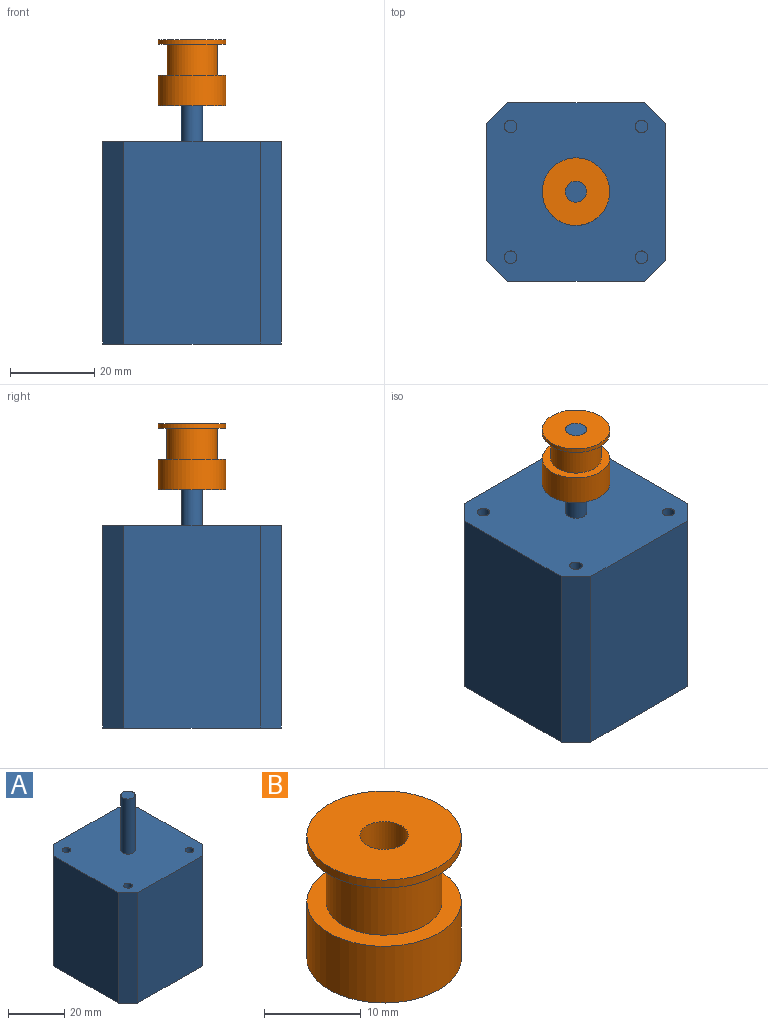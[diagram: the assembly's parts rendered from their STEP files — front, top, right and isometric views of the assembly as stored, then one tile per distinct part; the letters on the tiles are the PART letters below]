
ASSEMBLY  parts=2 mates=1
PART A: 20 faces, bbox 42.3x42.3x72 mm
  f0: plane 48x32.3mm, normal (0,-1,0), area 1550.4mm2, adj f4,f5,f7,f8
  f1: plane 48x32.3mm, normal (1,0,0), area 1550.4mm2, adj f4,f5,f8,f9
  f2: plane 48x32.3mm, normal (0,1,0), area 1550.4mm2, adj f4,f5,f6,f9
  f3: plane 48x32.3mm, normal (-1,0,0), area 1550.4mm2, adj f4,f5,f6,f7
  f4: plane 42.3x42.3mm, normal (0,0,1), area 1691.4mm2, adj f0,f1,f2,f3,f6,f7,f8,f9
  f5: plane 42.3x42.3mm, normal (0,0,-1), area 1739.3mm2, adj f0,f1,f2,f3,f6,f7,f8,f9
  f6: plane 48x5mm, normal (-0.71,0.71,0), area 339.4mm2, adj f2,f3,f4,f5
  f7: plane 48x5mm, normal (-0.71,-0.71,0), area 339.4mm2, adj f0,f3,f4,f5
  f8: plane 48x5mm, normal (0.71,-0.71,0), area 339.4mm2, adj f0,f1,f4,f5
  f9: plane 48x5mm, normal (0.71,0.71,0), area 339.4mm2, adj f1,f2,f4,f5
  f10: cylinder r=2.5mm len=24mm, axis (0,0,-1), area 377mm2, adj f4,f11
  f11: plane 5x5mm, normal (0,0,1), area 19.6mm2, adj f10
  f12: cylinder r=1.5mm len=20mm, axis (0,0,1), area 188.5mm2, adj f4,f13
  f13: plane 3x3mm, normal (0,0,1), area 7.1mm2, adj f12
  f14: cylinder r=1.5mm len=20mm, axis (0,0,1), area 188.5mm2, adj f4,f15
  f15: plane 3x3mm, normal (0,0,1), area 7.1mm2, adj f14
  f16: cylinder r=1.5mm len=20mm, axis (0,0,1), area 188.5mm2, adj f4,f17
  f17: plane 3x3mm, normal (0,0,1), area 7.1mm2, adj f16
  f18: cylinder r=1.5mm len=20mm, axis (0,0,1), area 188.5mm2, adj f4,f19
  f19: plane 3x3mm, normal (0,0,1), area 7.1mm2, adj f18
PART B: 8 faces, bbox 16x16x15.6 mm
  f0: cylinder r=8mm len=16mm, axis (0,0,-1), area 361.9mm2, adj f1,f2
  f1: plane 16x16mm, normal (0,0,1), area 88mm2, adj f0,f3
  f2: plane 16x16mm, normal (0,0,-1), area 181.4mm2, adj f0,f7
  f3: cylinder r=6mm len=12mm, axis (0,0,-1), area 279mm2, adj f1,f6
  f4: cylinder r=8mm len=16mm, axis (0,0,-1), area 50.3mm2, adj f5,f6
  f5: plane 16x16mm, normal (0,0,1), area 181.4mm2, adj f4,f7
  f6: plane 16x16mm, normal (0,0,-1), area 88mm2, adj f3,f4
  f7: cylinder r=2.5mm len=15.6mm, axis (0,0,1), area 245mm2, adj f2,f5
PLACE A t=(-20.12,-1.72,11.78)mm
PLACE B t=(-65.07,-1.72,68.18)mm
MATE fastened B.f0 <-> A.f10  axis (0,0,1) through (-20.12,-1.72,83.78)mm
